# Revit family: LEGRAND_NON INTERLOCKED SOCKETS_SURFACE MOUNTED_IP66_110
name_source: partatom
category: Installations électriques
revit_build: Autodesk Revit 2018 (Build: 20170223_1515(x64)
units: mm (PartAtom-declared; Revit-internal decimal feet)

## family parameters
Conserver l'orientation des annotations = Non
Cote de connecteur circulaire = Utiliser le diamètre
Couper avec des vides une fois chargée = Non
Hôte = Face
Partagée = Non
Point de calcul de pièce = Non
Type d'élément = Normal

## types (2) — shared parameters
Description = international standard socket for flush or surface mounting with accessory allows the connection of power devices
Dia bouchon = 68 mm
Elévation par défaut = 1000 mm  [stored 3.28084 ft]
Fabricant = Legrand
Flush E or Surface mounting S = flush and surface mounting
General Conditions of Use = https://export.legrand.com
Maximum installation temperature = 40°C
Maximum use temperature = 100°C
Minimum installation temperature = -20°C
Minimum use temperature = -50°C
Modèle = 051125
Number of poles = 3
Position of earth h = 4
RAY BOUCHON = 34 mm
Ray = 21 mm  [stored 0.0688976 ft]
Standard IEC or NFC = IEC
Tension V = 110 V  50/60 Hz yellow
characteristic color = yellow
connecting type = screw terminals
dIA = 42 mm  [stored 0.137795 ft]
halogen free = Non
horizontal fixing distance mm = 52 mm
intensity A = 16 A
material of box = plastic
protection class IP = IP66/67-55
resistance to chocks IK = 09
vertical fixing distance mm = 60 mm

## per-type parameters (varying)
| type | depth for flush mounting mm | depth mm | h1 | height mm | width mm |
| panel mounting socket IP66/67-55   16A   110 V   2P+E   plast surface mounting | 58 mm | 103 mm | 64 mm | 106 mm | 74 mm |
| panel mounting socket IP 66/67-55   16A   110 V   2P+E   plast surface box for passage wiring | 75 mm | 120 mm  [stored 0.393701 ft] | 109 mm | 182 mm | 86 mm |

note: [stored X ft] marks values corroborated as IEEE doubles in the binary element streams (Revit-internal decimal feet)
